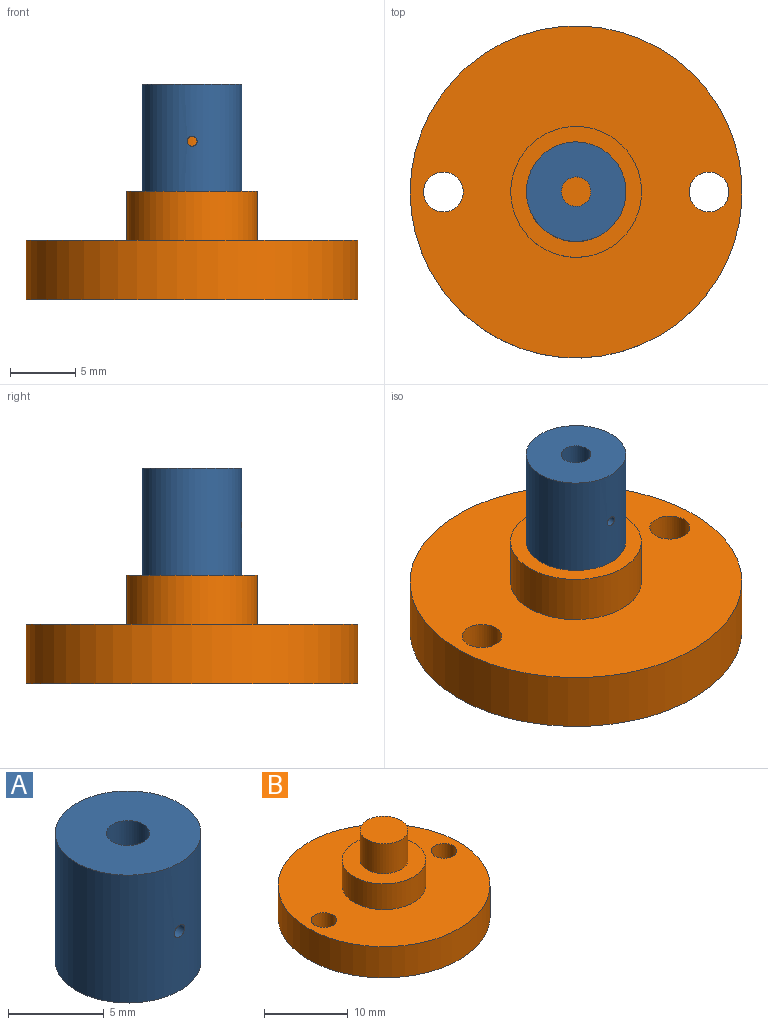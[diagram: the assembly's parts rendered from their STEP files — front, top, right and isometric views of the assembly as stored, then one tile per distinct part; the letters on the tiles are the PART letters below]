
ASSEMBLY  parts=2 mates=1
PART A: 7 faces, bbox 7.6x7.6x8.2 mm
  f0: cylinder r=2.87mm len=5.74mm, axis (0,0,1), area 78.3mm2, adj f2,f4,f5
  f1: cylinder r=3.81mm len=8.18mm, axis (0,0,1), area 195.3mm2, adj f2,f3,f5
  f2: plane 7.62x7.62mm, normal (0,0,-1), area 19.7mm2, adj f0,f1
  f3: plane 7.62x7.62mm, normal (0,0,1), area 41.6mm2, adj f1,f6
  f4: plane 5.74x5.74mm, normal (0,0,-1), area 21.9mm2, adj f0,f6
  f5: cylinder r=0.38mm len=0.97mm, axis (0,1,0), area 2.3mm2, adj f0,f1
  f6: cylinder r=1.13mm len=3.81mm, axis (0,0,1), area 27.1mm2, adj f3,f4
PART B: 9 faces, bbox 25.4x25.4x12.7 mm
  f0: cylinder r=2.87mm len=5.74mm, axis (0,0,-1), area 78.8mm2, adj f1,f6
  f1: plane 5.74x5.74mm, normal (0,0,1), area 25.9mm2, adj f0
  f2: plane 25.4x25.4mm, normal (0,0,-1), area 492.1mm2, adj f3,f7,f8
  f3: cylinder r=12.7mm len=25.4mm, axis (0,0,-1), area 364.8mm2, adj f2,f4
  f4: plane 25.4x25.4mm, normal (0,0,1), area 413.5mm2, adj f3,f5,f7,f8
  f5: cylinder r=5mm len=10.01mm, axis (0,0,-1), area 118.2mm2, adj f4,f6
  f6: plane 10.01x10.01mm, normal (0,0,1), area 52.8mm2, adj f0,f5
  f7: cylinder r=1.52mm len=4.57mm, axis (0,0,-1), area 43.8mm2, adj f2,f4
  f8: cylinder r=1.52mm len=4.57mm, axis (0,0,-1), area 43.8mm2, adj f2,f4
PLACE A t=(0,0,25.4)mm
PLACE B t=(0,0,17.07)mm
MATE fastened B.f0 <-> A.f0  axis (0,0,1) through (0,0,25.4)mm
